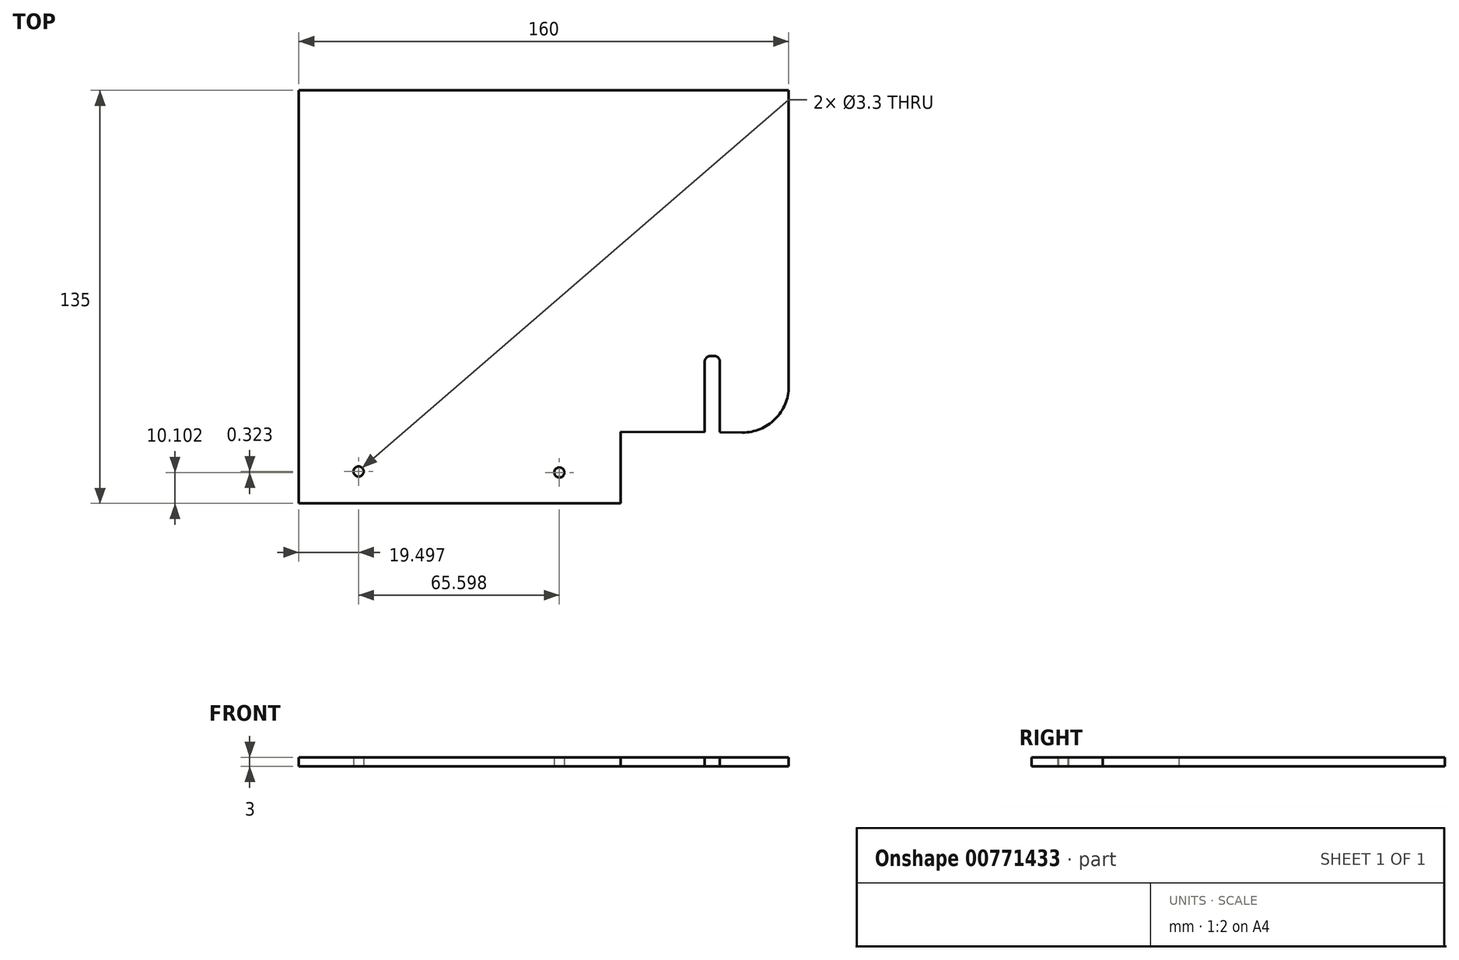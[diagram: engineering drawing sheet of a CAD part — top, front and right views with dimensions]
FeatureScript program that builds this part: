
annotation { "Feature Type Name" : "Feature", "Feature Type Description" : "" }
export const myFeature = defineFeature(function(context is Context, id is Id, definition is map)
    precondition{}
    {
        {
            var Q0;
            Q0=qCreatedBy(makeId("Top.planeOp"),FACE);
            var sketch = newSketch(context, id + "F0", { "sketchPlane" : qUnion([Q0])});
            skLineSegment(sketch, "E0.bottom", {"start": v(-49.82, 34.2) * mm, "end": v(110.18, 34.2) * mm});
            skLineSegment(sketch, "E0.top", {"start": v(-49.82, -100.8) * mm, "end": v(55.27, -100.8) * mm});
            skLineSegment(sketch, "E0.left", {"start": v(-49.82, 34.2) * mm, "end": v(-49.82, -100.8) * mm});
            skLineSegment(sketch, "E0.right", {"start": v(110.18, 34.2) * mm, "end": v(110.18, -77.74) * mm});
            skLineSegment(sketch, "E1", {"start": v(-49.72, -100.3) * mm, "end": v(55.27, -100.8) * mm});
            skLineSegment(sketch, "E2", {"start": v(55.27, -100.8) * mm, "end": v(55.27, -77.47) * mm});
            skLineSegment(sketch, "E3", {"start": v(55.27, -77.47) * mm, "end": v(82.73, -77.6) * mm});
            skLineSegment(sketch, "E4", {"start": v(82.73, -77.6) * mm, "end": v(82.73, -52.6) * mm});
            skLineSegment(sketch, "E5", {"start": v(82.73, -52.6) * mm, "end": v(87.73, -52.63) * mm});
            skLineSegment(sketch, "E6", {"start": v(87.73, -52.63) * mm, "end": v(87.73, -77.6) * mm});
            skLineSegment(sketch, "E7", {"start": v(87.73, -77.6) * mm, "end": v(110.18, -77.74) * mm});
            skLineSegment(sketch, "E8", {"start": v(-49.72, -100.3) * mm, "end": v(-30.32, -100.39) * mm});
            skLineSegment(sketch, "E9", {"start": v(-30.32, -100.39) * mm, "end": v(-30.32, -90.39) * mm});
            skPoint(sketch, "E10", {"position": v(-30.32, -90.39) * mm});
            skLineSegment(sketch, "E11", {"start": v(55.27, -100.8) * mm, "end": v(35.27, -100.7) * mm});
            skLineSegment(sketch, "E12", {"start": v(35.27, -100.7) * mm, "end": v(35.27, -90.7) * mm});
            skPoint(sketch, "E13", {"position": v(35.27, -90.7) * mm});
            skSolve(sketch);
        }
        {
            var Q0;
            Q0 = qSketchRegion(id + "F0", true);
            extrude(context, id + "F1", {"entities" : qUnion([Q0]), "depth" : 3 * mm, "offsetDistance" : 25 * mm});
        }
        {
            var Q0;
            Q0=makeQuery(id+"F1.opExtrude","SWEPT_EDGE",EDGE,{"disambiguationData":[OSD([sQuery(id+"F0.wireOp",EDGE,"E4"),sQuery(id+"F0.wireOp",EDGE,"E5")])]});
            fillet(context, id + "F2", {"entities" : qUnion([Q0]), "radius" : 2 * mm, "tangentPropagation" : true, "allowEdgeOverflow" : false});
        }
        {
            var Q0;
            Q0=makeQuery(id+"F1.opExtrude","SWEPT_EDGE",EDGE,{"disambiguationData":[OSD([sQuery(id+"F0.wireOp",EDGE,"E5"),sQuery(id+"F0.wireOp",EDGE,"E6")])]});
            fillet(context, id + "F3", {"entities" : qUnion([Q0]), "radius" : 2 * mm, "tangentPropagation" : true, "allowEdgeOverflow" : false});
        }
        {
            var Q0;
            Q0=sQuery(id+"F0.wireOp",VERTEX,"E10");
            var Q1;
            Q1=sQuery(id+"F0.wireOp",VERTEX,"E13");
            var Q2;
            Q2=makeQuery(id+"F1.opExtrude","SWEPT_BODY",BODY,{"disambiguationData":[OSD([sQuery(id+"F0.wireOp",EDGE,"E0.bottom"),sQuery(id+"F0.wireOp",EDGE,"E0.top"),sQuery(id+"F0.wireOp",EDGE,"E0.left"),sQuery(id+"F0.wireOp",EDGE,"E0.right"),sQuery(id+"F0.wireOp",EDGE,"E2"),sQuery(id+"F0.wireOp",EDGE,"E3"),sQuery(id+"F0.wireOp",EDGE,"E4"),sQuery(id+"F0.wireOp",EDGE,"E5"),sQuery(id+"F0.wireOp",EDGE,"E6"),sQuery(id+"F0.wireOp",EDGE,"E7")])]});
            hole(context, id + "F4", {"style" : HoleStyle.SIMPLE, "endStyle" : HoleEndStyle.THROUGH, "oppositeDirection" : true, "standardTappedOrClearance" : lookupTablePath({ "standard" : "ISO", "fit" : "Normal", "size" : "M3", "type" : "Clearance" }), "standardBlindInLast" : lookupTablePath({ "fit" : "Standard", "standard" : "ISO", "size" : "M3", "type" : "Clearance" }), "holeDiameter" : 3.3 * mm, "majorDiameter" : 5 * mm, "isTappedThrough" : true, "tappedDepth" : 12 * mm, "tapClearance" : 3, "locations" : qUnion([Q0, Q1]), "scope" : qUnion([Q2])});
        }
        {
            var Q0;
            Q0=makeQuery(id+"F1.opExtrude","SWEPT_EDGE",EDGE,{"disambiguationData":[OSD([sQuery(id+"F0.wireOp",EDGE,"E0.right"),sQuery(id+"F0.wireOp",EDGE,"E7")])]});
            fillet(context, id + "F5", {"entities" : qUnion([Q0]), "radius" : 15 * mm, "tangentPropagation" : true, "allowEdgeOverflow" : false});
        }
    });
